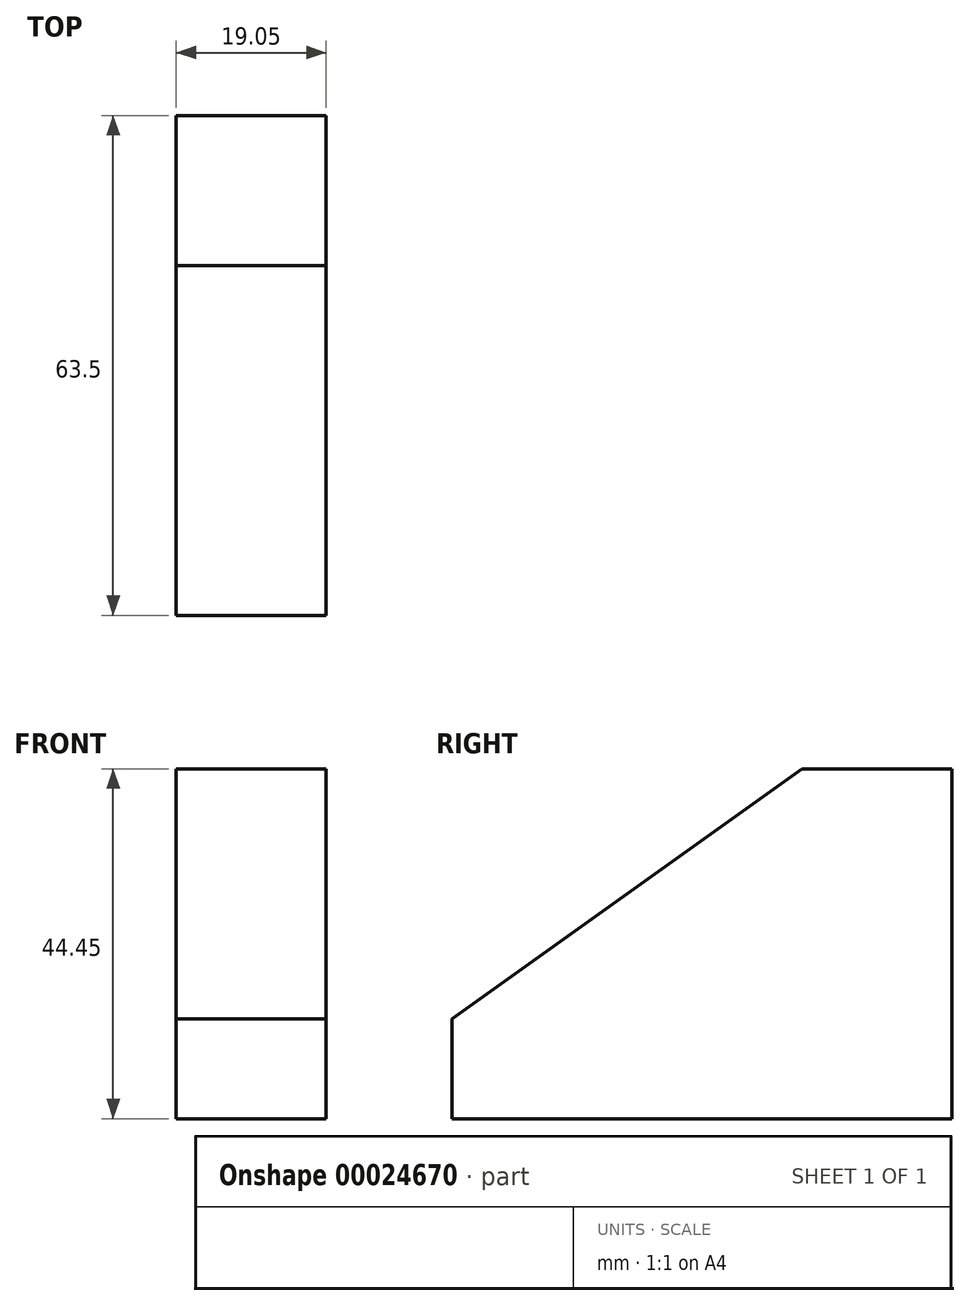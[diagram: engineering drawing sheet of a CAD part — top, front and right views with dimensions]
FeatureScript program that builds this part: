
annotation { "Feature Type Name" : "Feature", "Feature Type Description" : "" }
export const myFeature = defineFeature(function(context is Context, id is Id, definition is map)
    precondition{}
    {
        {
            var Q0;
            Q0=qCreatedBy(makeId("Right.planeOp"),FACE);
            var sketch = newSketch(context, id + "F0", { "sketchPlane" : qUnion([Q0])});
            skLineSegment(sketch, "E0", {"start": v(-73.45, 39.17) * mm, "end": v(-73.45, -5.28) * mm});
            skLineSegment(sketch, "E1.MirrorCS", {"start": v(-73.45, 39.17) * mm, "end": v(-92.5, 39.17) * mm});
            skLineSegment(sketch, "E2.MirrorCS", {"start": v(-136.95, 7.42) * mm, "end": v(-92.5, 39.17) * mm});
            skLineSegment(sketch, "E3.MirrorCS", {"start": v(-136.95, 7.42) * mm, "end": v(-136.95, -5.28) * mm});
            skLineSegment(sketch, "E4.MirrorCS", {"start": v(-73.45, -5.28) * mm, "end": v(-136.95, -5.28) * mm});
            skSolve(sketch);
        }
        {
            var Q0;
            Q0 = qSketchRegion(id + "F0", true);
            extrude(context, id + "F1", {"entities" : qUnion([Q0]), "depth" : 19.05 * mm});
        }
    });
